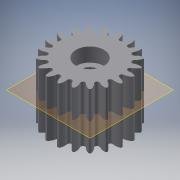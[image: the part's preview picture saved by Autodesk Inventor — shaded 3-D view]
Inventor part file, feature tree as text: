
AUTODESK INVENTOR PART (.ipt)
format: ipt  version: 2017 (Build 210142000, 142)  size: 269,824 bytes
history: native  units: mm
features: extrude x4, sketch x3, pattern_circular x1, plane x1, mirror x1
ambient origin geometry x8: Origin, YZ Plane, XZ Plane, XY Plane, X Axis, Y Axis, Z Axis, Center Point
bodies: Solid1 (feature_tree)
feature tree (10):
  sketch  "Sketch1"  dims[d0=20.0mm d1=0.0mm]
  extrude  "Extrusion1"  TaperAngle=0.0deg  [1 undecoded]
  extrude  "Extrusion2"  Depth=10.0mm TaperAngle=360.0deg
  pattern_circular  "Circular Pattern1"  [2 undecoded]
  extrude  "Extrusion3"  Depth=5.0mm
  extrude  "Extrusion4"  Depth=5.0mm TaperAngle=0.0deg
  plane  "Work Plane1"
  mirror  "Mirror1"
  sketch  "Sketch2"  dims[d2=10.0mm d3=0.0mm d4=200.0mm d5=360.0deg]
  sketch  "Sketch3"  dims[d7=10.0mm d8=5.0mm d9=0.0mm d10=6.0mm d11=5.0mm d12=0.0mm]
note: 3 required parameter values undecoded (feature->parameter linkage not recoverable at this tier; creation-order binding heuristic only, values carry confidence <= 0.55)
